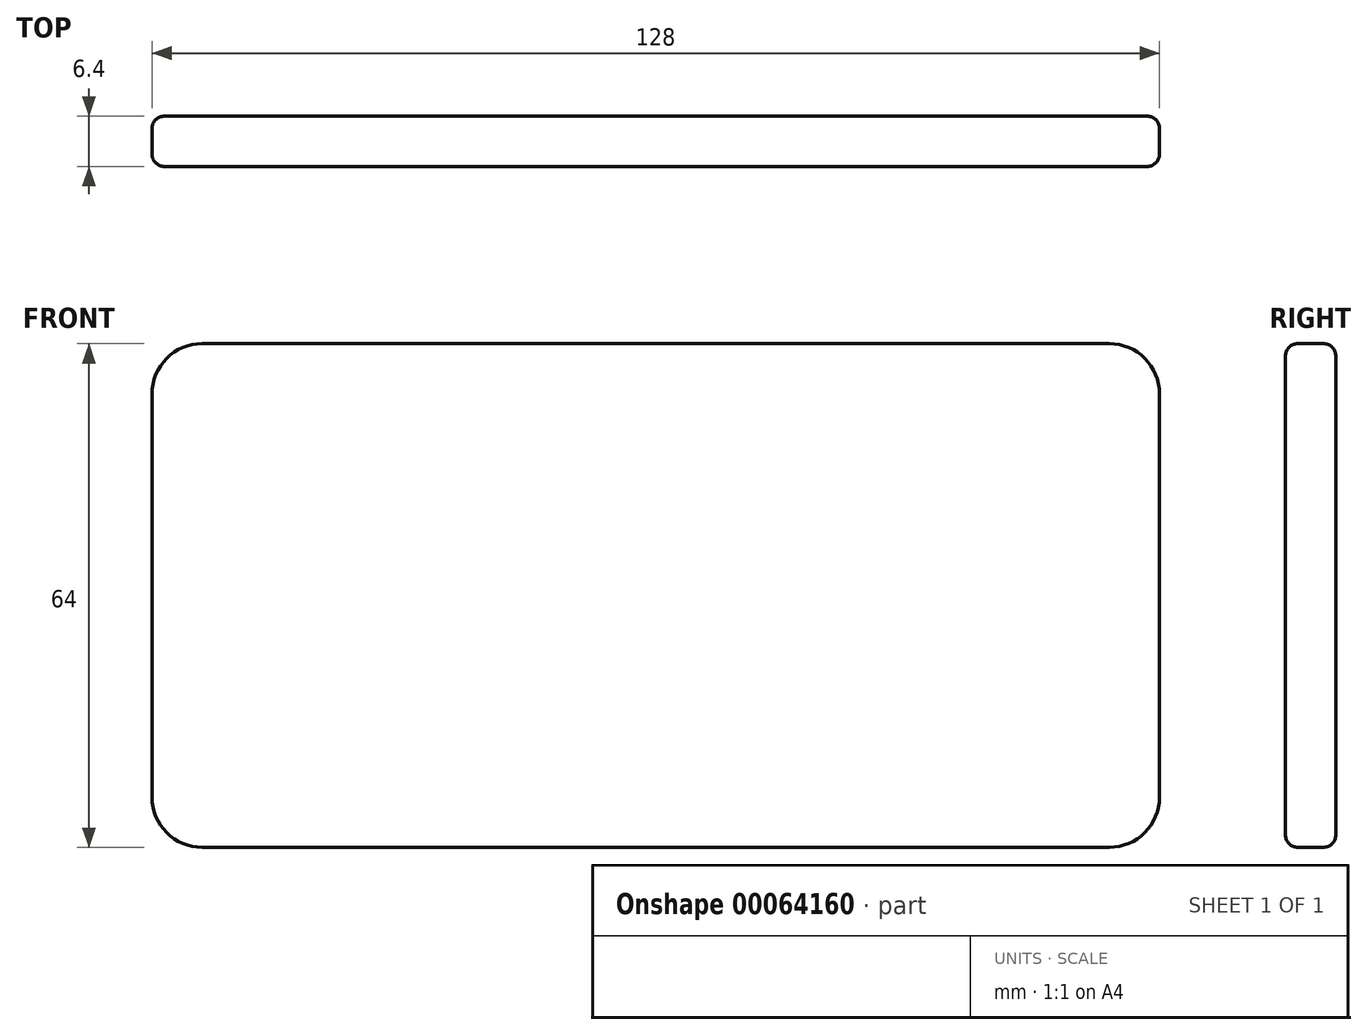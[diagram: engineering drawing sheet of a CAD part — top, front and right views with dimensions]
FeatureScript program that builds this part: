
annotation { "Feature Type Name" : "Feature", "Feature Type Description" : "" }
export const myFeature = defineFeature(function(context is Context, id is Id, definition is map)
    precondition{}
    {
        {
            var Q0;
            Q0=qCreatedBy(makeId("Front.planeOp"),FACE);
            var sketch = newSketch(context, id + "F0", { "sketchPlane" : qUnion([Q0])});
            skLineSegment(sketch, "E0.bottom", {"start": v(-64, 32) * mm, "end": v(64, 32) * mm});
            skLineSegment(sketch, "E0.top", {"start": v(-64, -32) * mm, "end": v(64, -32) * mm});
            skLineSegment(sketch, "E0.left", {"start": v(-64, 32) * mm, "end": v(-64, -32) * mm});
            skLineSegment(sketch, "E0.right", {"start": v(64, 32) * mm, "end": v(64, -32) * mm});
            skSolve(sketch);
        }
        {
            var Q0;
            Q0=makeQuery(id+"F0.imprint","IMPRINT",FACE,{"disambiguationData":[TD([[makeQuery(id+"F0.imprint","IMPRINT",EDGE,{"derivedFrom":sQuery(id+"F0.wireOp",EDGE,"E0.bottom")}),-1.0]])]});
            extrude(context, id + "F1", {"entities" : qUnion([Q0]), "oppositeDirection" : true, "depth" : 6.4 * mm});
        }
        {
            var Q0;
            Q0=makeQuery(id+"F1.opExtrude","SWEPT_EDGE",EDGE,{"disambiguationData":[OSD([sQuery(id+"F0.wireOp",EDGE,"E0.bottom"),sQuery(id+"F0.wireOp",EDGE,"E0.right")])]});
            var Q1;
            Q1=makeQuery(id+"F1.opExtrude","SWEPT_EDGE",EDGE,{"disambiguationData":[OSD([sQuery(id+"F0.wireOp",EDGE,"E0.top"),sQuery(id+"F0.wireOp",EDGE,"E0.right")])]});
            var Q2;
            Q2=makeQuery(id+"F1.opExtrude","SWEPT_EDGE",EDGE,{"disambiguationData":[OSD([sQuery(id+"F0.wireOp",EDGE,"E0.bottom"),sQuery(id+"F0.wireOp",EDGE,"E0.left")])]});
            var Q3;
            Q3=makeQuery(id+"F1.opExtrude","SWEPT_EDGE",EDGE,{"disambiguationData":[OSD([sQuery(id+"F0.wireOp",EDGE,"E0.top"),sQuery(id+"F0.wireOp",EDGE,"E0.left")])]});
            fillet(context, id + "F2", {"entities" : qUnion([Q0, Q1, Q2, Q3]), "radius" : 6.4 * mm, "tangentPropagation" : true, "allowEdgeOverflow" : false});
        }
        {
            var Q0;
            Q0=makeQuery(id+"F1.opExtrude","CAP_FACE",FACE,{"disambiguationData":[OSD([sQuery(id+"F0.wireOp",EDGE,"E0.bottom"),sQuery(id+"F0.wireOp",EDGE,"E0.top"),sQuery(id+"F0.wireOp",EDGE,"E0.left"),sQuery(id+"F0.wireOp",EDGE,"E0.right")])],"isStart":true});
            var Q1;
            Q1=makeQuery(id+"F1.opExtrude","CAP_FACE",FACE,{"disambiguationData":[OSD([sQuery(id+"F0.wireOp",EDGE,"E0.bottom"),sQuery(id+"F0.wireOp",EDGE,"E0.top"),sQuery(id+"F0.wireOp",EDGE,"E0.left"),sQuery(id+"F0.wireOp",EDGE,"E0.right")])],"isStart":false});
            fillet(context, id + "F3", {"entities" : qUnion([Q0, Q1]), "radius" : 1.6 * mm, "tangentPropagation" : true, "allowEdgeOverflow" : false});
        }
    });
